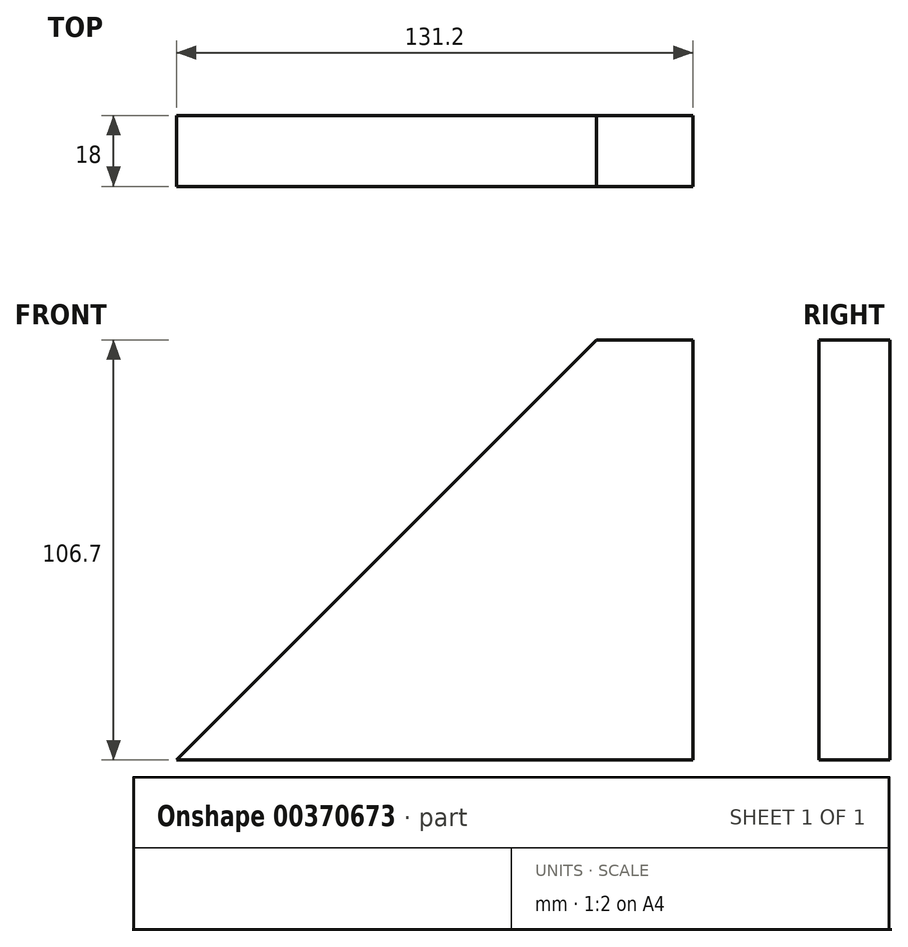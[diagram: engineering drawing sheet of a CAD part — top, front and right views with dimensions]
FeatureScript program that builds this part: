
annotation { "Feature Type Name" : "Feature", "Feature Type Description" : "" }
export const myFeature = defineFeature(function(context is Context, id is Id, definition is map)
    precondition{}
    {
        {
            var Q0;
            Q0=qCreatedBy(makeId("Front.planeOp"),FACE);
            var sketch = newSketch(context, id + "F0", { "sketchPlane" : qUnion([Q0])});
            skLineSegment(sketch, "E0", {"start": v(0, 0) * mm, "end": v(106.7, 106.7) * mm});
            skLineSegment(sketch, "E1", {"start": v(106.7, 106.7) * mm, "end": v(131.2, 106.7) * mm});
            skLineSegment(sketch, "E2", {"start": v(131.2, 106.7) * mm, "end": v(131.2, 0) * mm});
            skLineSegment(sketch, "E3", {"start": v(131.2, 0) * mm, "end": v(0, 0) * mm});
            skSolve(sketch);
        }
        {
            var Q0;
            Q0 = qSketchRegion(id + "F0", true);
            extrude(context, id + "F1", {"entities" : qUnion([Q0]), "depth" : 18 * mm});
        }
    });
